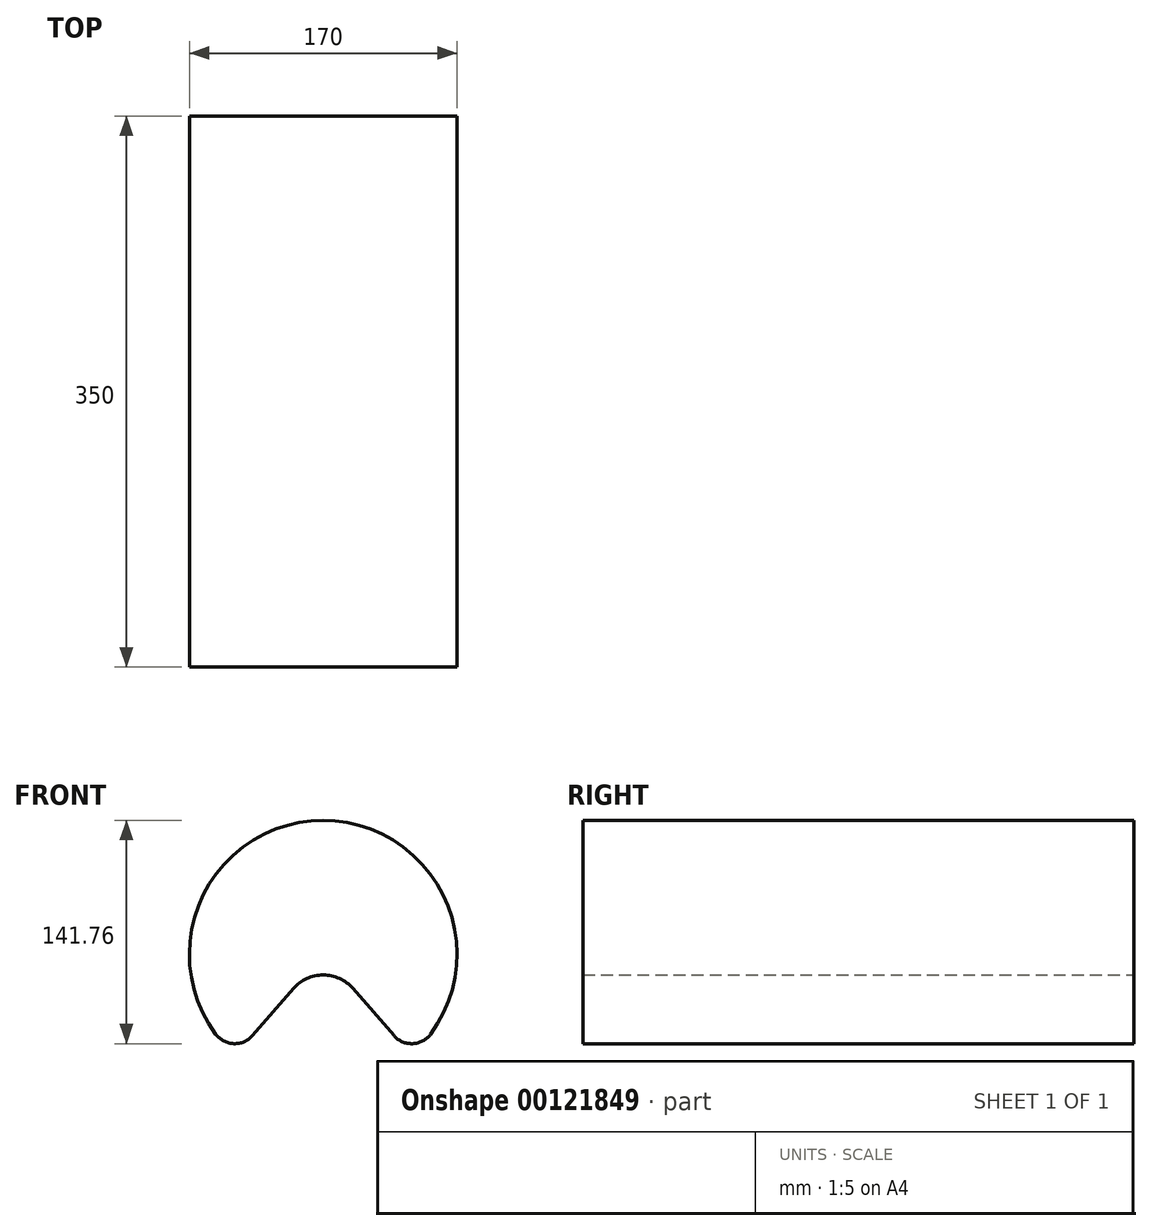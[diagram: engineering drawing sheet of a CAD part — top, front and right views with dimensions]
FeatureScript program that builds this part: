
annotation { "Feature Type Name" : "Feature", "Feature Type Description" : "" }
export const myFeature = defineFeature(function(context is Context, id is Id, definition is map)
    precondition{}
    {
        {
            var Q0;
            Q0=qCreatedBy(makeId("Front.planeOp"),FACE);
            var sketch = newSketch(context, id + "F0", { "sketchPlane" : qUnion([Q0])});
            skArc(sketch, "E0", {"start": v(68.22, -50.71) * mm, "mid": v(0, 85) * mm, "end": v(-68.22, -50.71) * mm});
            skLineSegment(sketch, "E1", {"start": v(0, 0) * mm, "end": v(0, -95.57) * mm, "construction": true});
            skLineSegment(sketch, "E2.MirrorCS", {"start": v(18.87, -21.7) * mm, "end": v(44.86, -51.6) * mm});
            skLineSegment(sketch, "E3.MirrorCS", {"start": v(-18.87, -21.7) * mm, "end": v(-44.86, -51.6) * mm});
            skPoint(sketch, "E4.orphan", {"position": v(55.77, -64.15) * mm});
            skArc(sketch, "E5.filletArc", {"start": v(18.87, -21.7) * mm, "mid": v(0, -13.1) * mm, "end": v(-18.87, -21.7) * mm});
            skPoint(sketch, "E6.visualSharp", {"position": v(-55.77, -64.15) * mm});
            skArc(sketch, "E6.filletArc", {"start": v(-68.22, -50.71) * mm, "mid": v(-56.75, -56.75) * mm, "end": v(-44.86, -51.6) * mm});
            skArc(sketch, "E7.filletArc", {"start": v(44.86, -51.6) * mm, "mid": v(56.75, -56.75) * mm, "end": v(68.22, -50.71) * mm});
            skLineSegment(sketch, "E8", {"start": v(-56.18, -41.76) * mm, "end": v(-58.32, -56.6) * mm, "construction": true});
            skLineSegment(sketch, "E9", {"start": v(-58.32, -56.6) * mm, "end": v(-52.42, -57.46) * mm, "construction": true});
            skSolve(sketch);
        }
        {
            var Q0;
            Q0=makeQuery(id+"F0.imprint","IMPRINT",FACE,{"disambiguationData":[TD([[makeQuery(id+"F0.imprint","IMPRINT",EDGE,{"derivedFrom":sQuery(id+"F0.wireOp",EDGE,"E0")}),1.0]])]});
            extrude(context, id + "F1", {"entities" : qUnion([Q0]), "endBound" : BoundingType.SYMMETRIC, "depth" : 350 * mm});
        }
        {
            var Q0;
            Q0=qCreatedBy(makeId("Front.planeOp"),FACE);
            var sketch = newSketch(context, id + "F2", { "sketchPlane" : qUnion([Q0])});
            skArc(sketch, "E10.0", {"start": v(-68.22, -50.71) * mm, "mid": v(-56.75, -56.75) * mm, "end": v(-44.86, -51.6) * mm});
            skArc(sketch, "E11.0", {"start": v(44.86, -51.6) * mm, "mid": v(56.75, -56.75) * mm, "end": v(68.22, -50.71) * mm});
            skLineSegment(sketch, "E12", {"start": v(-56.18, -41.76) * mm, "end": v(-52.02, -56.17) * mm, "construction": true});
            skLineSegment(sketch, "E13", {"start": v(56.18, -41.76) * mm, "end": v(60.77, -56.04) * mm, "construction": true});
            skPoint(sketch, "E14", {"position": v(-52.02, -56.17) * mm});
            skPoint(sketch, "E15", {"position": v(60.77, -56.04) * mm});
            skSolve(sketch);
        }
    });
